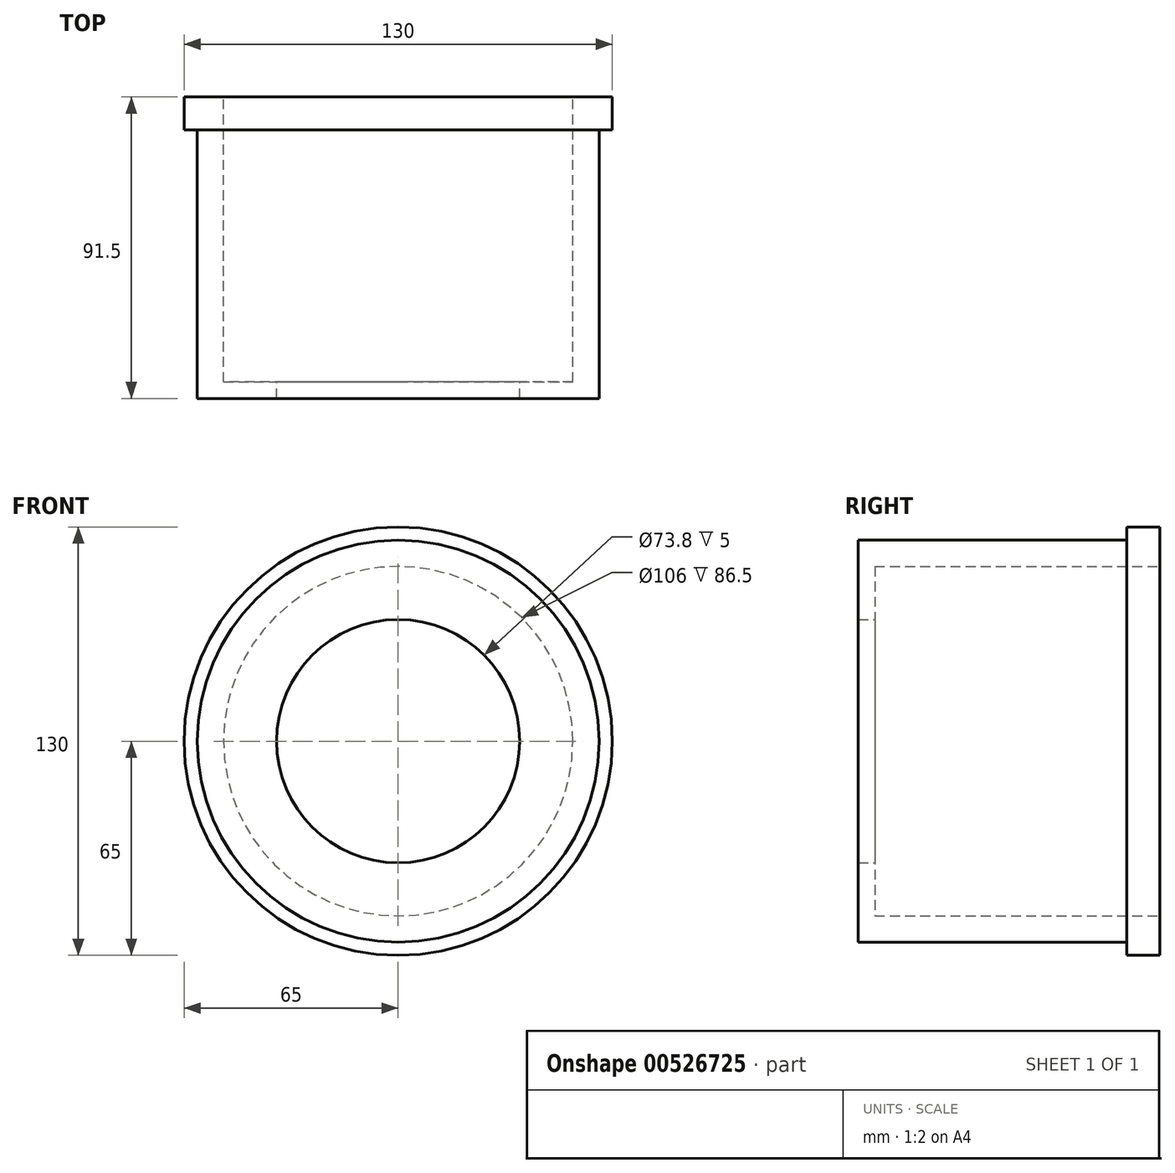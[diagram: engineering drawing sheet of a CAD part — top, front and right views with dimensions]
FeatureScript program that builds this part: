
annotation { "Feature Type Name" : "Feature", "Feature Type Description" : "" }
export const myFeature = defineFeature(function(context is Context, id is Id, definition is map)
    precondition{}
    {
        {
            var Q0;
            Q0=qCreatedBy(makeId("Top.planeOp"),FACE);
            var sketch = newSketch(context, id + "F0", { "sketchPlane" : qUnion([Q0])});
            skLineSegment(sketch, "E0.bottom", {"start": v(-65, -5) * mm, "end": v(-61, -5) * mm});
            skLineSegment(sketch, "E0.top", {"start": v(-65, 5) * mm, "end": v(-53, 5) * mm});
            skLineSegment(sketch, "E0.left", {"start": v(-65, -5) * mm, "end": v(-65, 5) * mm});
            skPoint(sketch, "E0.middle", {"position": v(0, 0) * mm});
            skLineSegment(sketch, "E1.left", {"start": v(-61, -86.5) * mm, "end": v(-61, -5) * mm});
            skLineSegment(sketch, "E2.left", {"start": v(-53, -81.5) * mm, "end": v(-53, 5) * mm});
            skPoint(sketch, "E2.top.start.orphan", {"position": v(-53, 81.5) * mm});
            skPoint(sketch, "E1.top.start.orphan", {"position": v(-61, 86.5) * mm});
            skPoint(sketch, "E3.orphan", {"position": v(53, 81.5) * mm});
            skPoint(sketch, "E4.orphan", {"position": v(61, 86.5) * mm});
            skLineSegment(sketch, "E5", {"start": v(0, 5) * mm, "end": v(0, -86.5) * mm, "construction": true});
            skPoint(sketch, "E6.orphan", {"position": v(53, -81.5) * mm});
            skPoint(sketch, "E7.orphan", {"position": v(61, -86.5) * mm});
            skPoint(sketch, "E0.right.end.orphan", {"position": v(65, 5) * mm});
            skPoint(sketch, "E0.right.start.orphan", {"position": v(65, -5) * mm});
            skLineSegment(sketch, "E8", {"start": v(-36.9, -81.5) * mm, "end": v(-36.9, -86.5) * mm});
            skLineSegment(sketch, "E9", {"start": v(-61, -86.5) * mm, "end": v(-36.9, -86.5) * mm});
            skLineSegment(sketch, "E10", {"start": v(-36.9, -81.5) * mm, "end": v(-53, -81.5) * mm});
            skSolve(sketch);
        }
        {
            var Q0;
            Q0=qSketchRegion(id+"F0",true);
            var Q1;
            Q1=sQuery(id+"F0.wireOp",EDGE,"E5");
            revolve(context, id + "F1", {"entities" : qUnion([Q0]), "axis" : qUnion([Q1]), "revolveType" : RevolveType.FULL});
        }
    });
